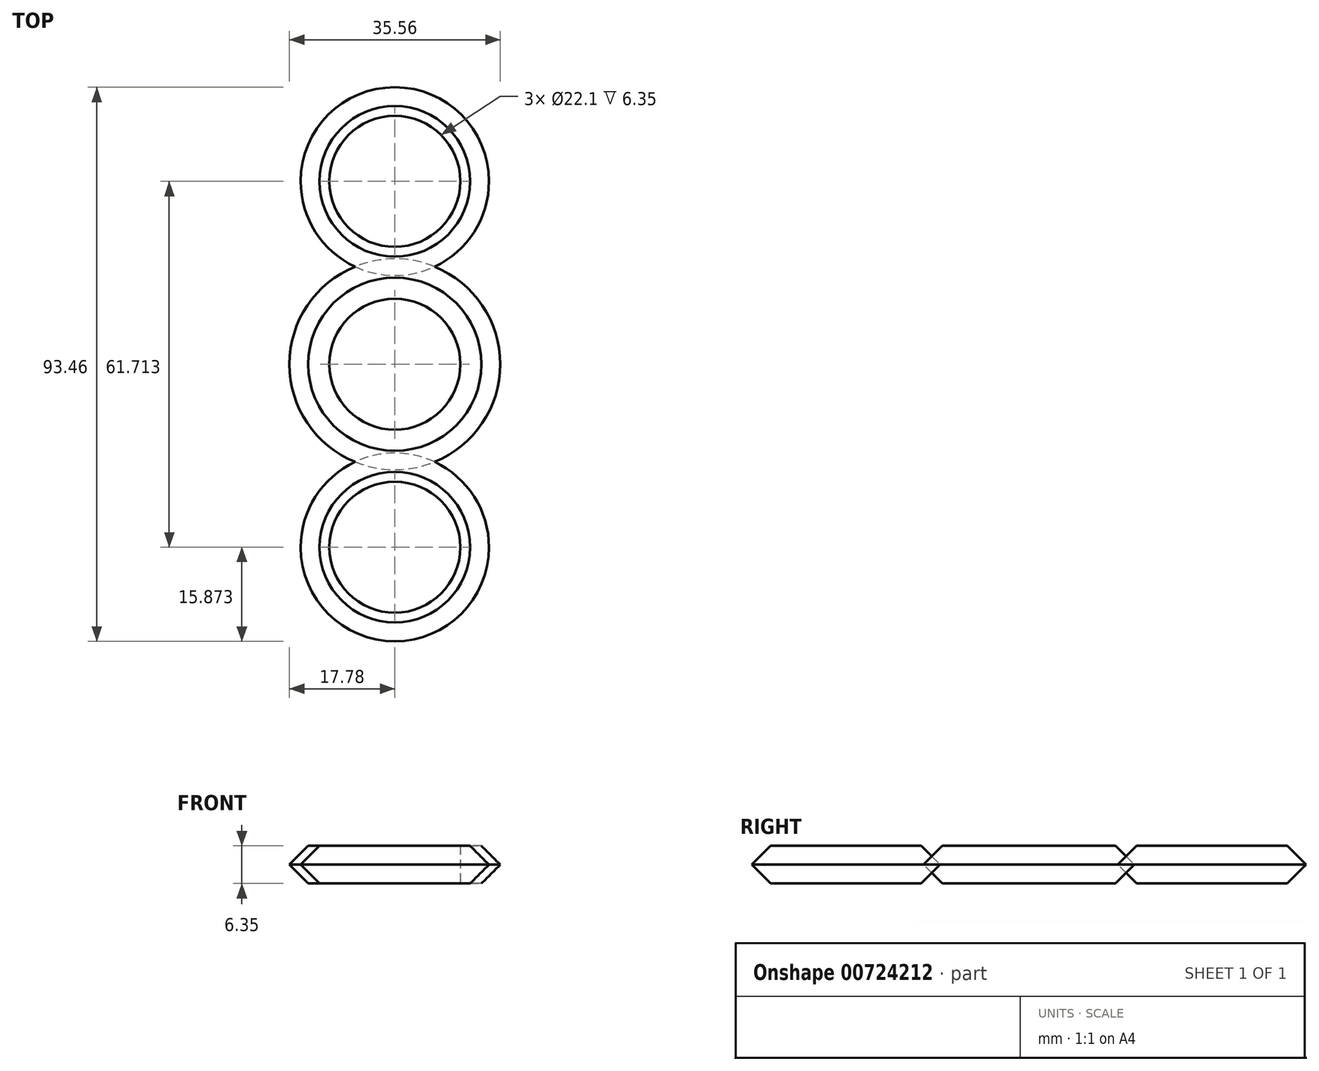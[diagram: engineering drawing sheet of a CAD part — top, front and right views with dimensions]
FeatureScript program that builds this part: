
annotation { "Feature Type Name" : "Feature", "Feature Type Description" : "" }
export const myFeature = defineFeature(function(context is Context, id is Id, definition is map)
    precondition{}
    {
        {
            var Q0;
            Q0=qCreatedBy(makeId("Top.planeOp"),FACE);
            var sketch = newSketch(context, id + "F0", { "sketchPlane" : qUnion([Q0])});
            skCircle(sketch, "E0", {"center": v(0, -30.86) * mm, "radius": 17.78 * mm});
            skCircle(sketch, "E1", {"center": v(0, -30.86) * mm, "radius": 11.05 * mm});
            skSolve(sketch);
        }
        {
            var Q0;
            Q0=qCreatedBy(makeId("Top.planeOp"),FACE);
            var sketch = newSketch(context, id + "F1", { "sketchPlane" : qUnion([Q0])});
            skCircle(sketch, "E2", {"center": v(0, 30.86) * mm, "radius": 17.78 * mm});
            skCircle(sketch, "E3", {"center": v(0, 30.86) * mm, "radius": 11.05 * mm});
            skSolve(sketch);
        }
        {
            var Q0;
            Q0=qCreatedBy(makeId("Top.planeOp"),FACE);
            var sketch = newSketch(context, id + "F2", { "sketchPlane" : qUnion([Q0])});
            skCircle(sketch, "E4", {"center": v(0, 0) * mm, "radius": 11.05 * mm});
            skCircle(sketch, "E5", {"center": v(0, 0) * mm, "radius": 19.69 * mm});
            skSolve(sketch);
        }
        {
            var Q0;
            Q0=makeQuery(id+"F1.imprint","IMPRINT",FACE,{"disambiguationData":[TD([[makeQuery(id+"F1.imprint","IMPRINT",EDGE,{"derivedFrom":sQuery(id+"F1.wireOp",EDGE,"E2")}),1.0]])]});
            var Q1;
            Q1=makeQuery(id+"F2.imprint","IMPRINT",FACE,{"disambiguationData":[TD([[makeQuery(id+"F2.imprint","IMPRINT",EDGE,{"derivedFrom":sQuery(id+"F2.wireOp",EDGE,"E4")}),-1.0]])]});
            var Q2;
            Q2=makeQuery(id+"F0.imprint","IMPRINT",FACE,{"disambiguationData":[TD([[makeQuery(id+"F0.imprint","IMPRINT",EDGE,{"derivedFrom":sQuery(id+"F0.wireOp",EDGE,"E0")}),1.0]])]});
            extrude(context, id + "F3", {"entities" : qUnion([Q0, Q1, Q2]), "depth" : 6.35 * mm, "offsetDistance" : 25.4 * mm});
        }
        {
            var Q0;
            Q0=makeQuery(id+"F3.opExtrude","CAP_EDGE",EDGE,{"disambiguationData":[OSD([sQuery(id+"F1.wireOp",EDGE,"E2")])],"isStart":true});
            var Q1;
            Q1=makeQuery(id+"F3.opExtrude","CAP_EDGE",EDGE,{"disambiguationData":[OSD([sQuery(id+"F2.wireOp",EDGE,"E5")])],"isStart":true});
            var Q2;
            Q2=makeQuery(id+"F3.opExtrude","CAP_EDGE",EDGE,{"disambiguationData":[OSD([sQuery(id+"F0.wireOp",EDGE,"E0")])],"isStart":true});
            chamfer(context, id + "F4", {"entities" : qUnion([Q0, Q1, Q2]), "width" : 5.08 * mm, "tangentPropagation" : true});
        }
        {
            var Q0;
            Q0=makeQuery(id+"F3.opExtrude","CAP_EDGE",EDGE,{"disambiguationData":[OSD([sQuery(id+"F1.wireOp",EDGE,"E2")])],"isStart":false});
            var Q1;
            Q1=makeQuery(id+"F3.opExtrude","CAP_EDGE",EDGE,{"disambiguationData":[OSD([sQuery(id+"F2.wireOp",EDGE,"E5")])],"isStart":false});
            var Q2;
            Q2=makeQuery(id+"F3.opExtrude","CAP_EDGE",EDGE,{"disambiguationData":[OSD([sQuery(id+"F0.wireOp",EDGE,"E0")])],"isStart":false});
            chamfer(context, id + "F5", {"entities" : qUnion([Q0, Q1, Q2]), "width" : 5.08 * mm, "tangentPropagation" : true});
        }
    });
